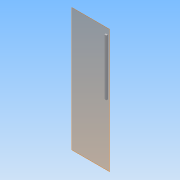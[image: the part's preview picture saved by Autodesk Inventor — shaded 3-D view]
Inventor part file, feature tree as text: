
AUTODESK INVENTOR PART (.ipt)
format: ipt  version: 2013 (Build 170138000, 138)  size: 81,408 bytes
history: native  units: in
note: dims shown in document units (in); Inventor stores cm internally (conversion verified against a paired STEP export)
features: extrude x2, sketch x2, plane x1
ambient origin geometry x8: Origin, YZ Plane, XZ Plane, XY Plane, X Axis, Y Axis, Z Axis, Center Point
bodies: Solid1 (feature_tree)
feature tree (5):
  plane  "Work Plane1"
  extrude  "Extrusion1"  Depth=1.5in
  extrude  "Extrusion2"  TaperAngle=0.0deg  [1 undecoded]
  sketch  "Sketch1"  dims[d0=39.0in d2=1.5in]
  sketch  "Sketch2"  dims[d3=1.0in d4=0.0in d5=38.5in d7=0.5in d8=0.3332in d9=0.0in]
note: 1 required parameter value undecoded (feature->parameter linkage not recoverable at this tier; creation-order binding heuristic only, values carry confidence <= 0.55)
